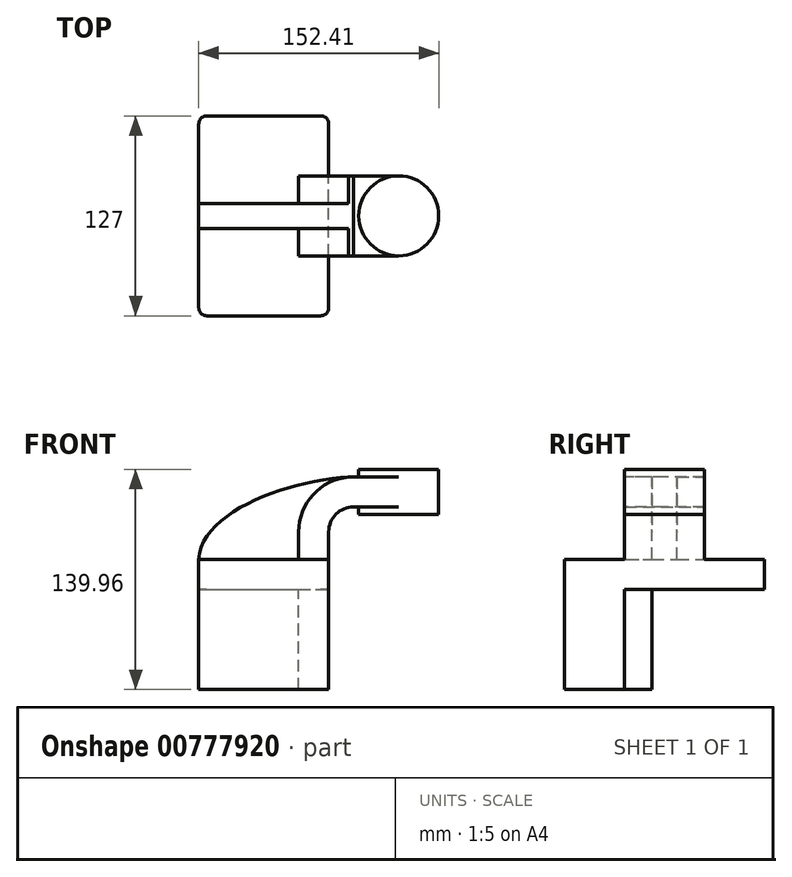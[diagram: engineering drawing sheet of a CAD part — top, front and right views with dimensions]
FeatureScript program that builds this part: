
annotation { "Feature Type Name" : "Feature", "Feature Type Description" : "" }
export const myFeature = defineFeature(function(context is Context, id is Id, definition is map)
    precondition{}
    {
        {
            var Q0;
            Q0=qCreatedBy(makeId("Front.planeOp"),FACE);
            var sketch = newSketch(context, id + "F0", { "sketchPlane" : qUnion([Q0])});
            skLineSegment(sketch, "E0.rect.bottom", {"start": v(-41.28, 9.52) * mm, "end": v(41.28, 9.52) * mm});
            skLineSegment(sketch, "E0.rect.top", {"start": v(-41.28, -9.52) * mm, "end": v(41.28, -9.52) * mm});
            skLineSegment(sketch, "E0.rect.left", {"start": v(-41.28, 9.52) * mm, "end": v(-41.28, -9.52) * mm});
            skLineSegment(sketch, "E0.rect.right", {"start": v(41.28, 9.52) * mm, "end": v(41.28, -9.52) * mm});
            skPoint(sketch, "E0.rect.middle", {"position": v(0, 0) * mm});
            skLineSegment(sketch, "E1", {"start": v(41.28, 9.52) * mm, "end": v(41.28, 27) * mm});
            skArc(sketch, "E2", {"start": v(41.28, 27) * mm, "mid": v(45.92, 38.23) * mm, "end": v(57.15, 42.88) * mm});
            skLineSegment(sketch, "E3", {"start": v(57.15, 42.88) * mm, "end": v(85.72, 42.88) * mm});
            skLineSegment(sketch, "E4.rect.bottom", {"start": v(60.32, 38.1) * mm, "end": v(111.12, 38.1) * mm});
            skLineSegment(sketch, "E4.rect.top", {"start": v(60.32, 66.68) * mm, "end": v(111.12, 66.68) * mm});
            skLineSegment(sketch, "E4.rect.left", {"start": v(60.32, 38.1) * mm, "end": v(60.32, 66.68) * mm});
            skLineSegment(sketch, "E4.rect.right", {"start": v(111.13, 38.1) * mm, "end": v(111.12, 66.68) * mm});
            skPoint(sketch, "E4.rect.middle", {"position": v(85.72, 52.39) * mm});
            skLineSegment(sketch, "E5.0", {"start": v(57.15, 61.93) * mm, "end": v(85.72, 61.93) * mm});
            skArc(sketch, "E5.1", {"start": v(22.23, 27) * mm, "mid": v(32.45, 51.7) * mm, "end": v(57.15, 61.93) * mm});
            skLineSegment(sketch, "E5.2", {"start": v(22.23, 9.52) * mm, "end": v(22.23, 27) * mm});
            skLineSegment(sketch, "E6", {"start": v(85.72, 38.1) * mm, "end": v(85.72, 66.68) * mm});
            skFitSpline(sketch, "E7", {"points": [v(-41.28, 9.53) * mm, v(57.15, 61.93) * mm], "startDerivative": vector(5.2, 92.34) * mm, "endDerivative": vector(120.92, 4.22) * mm});
            skSolve(sketch);
        }
        {
            var Q0;
            Q0=makeQuery(id+"F0.imprint","IMPRINT",FACE,{"disambiguationData":[TD([[makeQuery(id+"F0.imprint","IMPRINT",EDGE,{"derivedFrom":sQuery(id+"F0.wireOp",EDGE,"E0.rect.top")}),1.0]])]});
            extrude(context, id + "F1", {"entities" : qUnion([Q0]), "endBound" : BoundingType.SYMMETRIC, "depth" : 127 * mm});
        }
        {
            var Q0;
            {var subQ9=sQuery(id+"F0.wireOp",EDGE,"E1");Q0=makeQuery(id+"F0.imprint","IMPRINT",FACE,{"disambiguationData":[TD([[makeQuery(id+"F0.imprint","IMPRINT",EDGE,{"derivedFrom":subQ9}),1.0]])]});}
            var Q1;
            {var subQ0=sQuery(id+"F0.wireOp",EDGE,"E6");var subQ1=sQuery(id+"F0.wireOp",EDGE,"E3");var subQ2=makeQuery(id+"F0.imprint","INTERSECT",VERTEX,{"derivedFrom":[subQ1,subQ0]});Q1=makeQuery(id+"F0.imprint","IMPRINT",FACE,{"disambiguationData":[TD([[makeQuery(id+"F0.imprint","IMPRINT",EDGE,{"disambiguationData":[TD([[subQ2,1.0]])],"derivedFrom":subQ1}),1.0]])]});}
            extrude(context, id + "F2", {"entities" : qUnion([Q0, Q1]), "operationType" : NewBodyOperationType.ADD, "endBound" : BoundingType.SYMMETRIC, "depth" : 50.8 * mm});
        }
        {
            var Q0;
            {var subQ3=sQuery(id+"F0.wireOp",EDGE,"E5.2");Q0=makeQuery(id+"F0.imprint","IMPRINT",FACE,{"disambiguationData":[TD([[makeQuery(id+"F0.imprint","IMPRINT",EDGE,{"derivedFrom":subQ3}),1.0]])]});}
            extrude(context, id + "F3", {"entities" : qUnion([Q0]), "operationType" : NewBodyOperationType.ADD, "endBound" : BoundingType.SYMMETRIC, "depth" : 15.88 * mm});
        }
        {
            var Q0;
            {var subQ5=sQuery(id+"F0.wireOp",EDGE,"E4.rect.right");Q0=makeQuery(id+"F0.imprint","IMPRINT",FACE,{"disambiguationData":[TD([[makeQuery(id+"F0.imprint","IMPRINT",EDGE,{"derivedFrom":subQ5}),1.0]])]});}
            var Q1;
            Q1=sQuery(id+"F0.wireOp",EDGE,"E6");
            revolve(context, id + "F4", {"operationType" : NewBodyOperationType.ADD, "entities" : qUnion([Q0]), "axis" : qUnion([Q1]), "revolveType" : RevolveType.FULL});
        }
        {
            var Q0;
            Q0=makeQuery(id+"F1.opExtrude","CAP_EDGE",EDGE,{"disambiguationData":[OSD([sQuery(id+"F0.wireOp",EDGE,"E0.rect.right")])],"isStart":false});
            var Q1;
            Q1=makeQuery(id+"F1.opExtrude","CAP_EDGE",EDGE,{"disambiguationData":[OSD([sQuery(id+"F0.wireOp",EDGE,"E0.rect.left")])],"isStart":false});
            var Q2;
            Q2=makeQuery(id+"F1.opExtrude","CAP_EDGE",EDGE,{"disambiguationData":[OSD([sQuery(id+"F0.wireOp",EDGE,"E0.rect.right")])],"isStart":true});
            var Q3;
            Q3=makeQuery(id+"F1.opExtrude","CAP_EDGE",EDGE,{"disambiguationData":[OSD([sQuery(id+"F0.wireOp",EDGE,"E0.rect.left")])],"isStart":true});
            fillet(context, id + "F5", {"entities" : qUnion([Q0, Q1, Q2, Q3]), "radius" : 5.08 * mm, "tangentPropagation" : true, "allowEdgeOverflow" : false});
        }
        {
            var Q0;
            {var subQ4=sQuery(id+"F0.wireOp",EDGE,"E0.rect.bottom");var subQ5=sQuery(id+"F0.wireOp",EDGE,"E0.rect.right");var subQ6=sQuery(id+"F0.wireOp",EDGE,"E0.rect.left");Q0=makeQuery(id+"F3.boolean.opBoolean","SPLIT",FACE,{"disambiguationData":[TD([makeQuery(id+"F1.opExtrude","CAP_FACE",FACE,{"disambiguationData":[OSD([subQ4,sQuery(id+"F0.wireOp",EDGE,"E0.rect.top"),subQ6,subQ5])],"isStart":false})])],"derivedFrom":makeQuery(id+"F1.opExtrude","SWEPT_FACE",FACE,{"disambiguationData":[OSD([subQ4])]})});}
            extrude(context, id + "F6", {"entities" : qUnion([Q0]), "operationType" : NewBodyOperationType.ADD, "oppositeDirection" : true, "depth" : 82.8 * mm, "offsetDistance" : 25.4 * mm});
        }
    });
